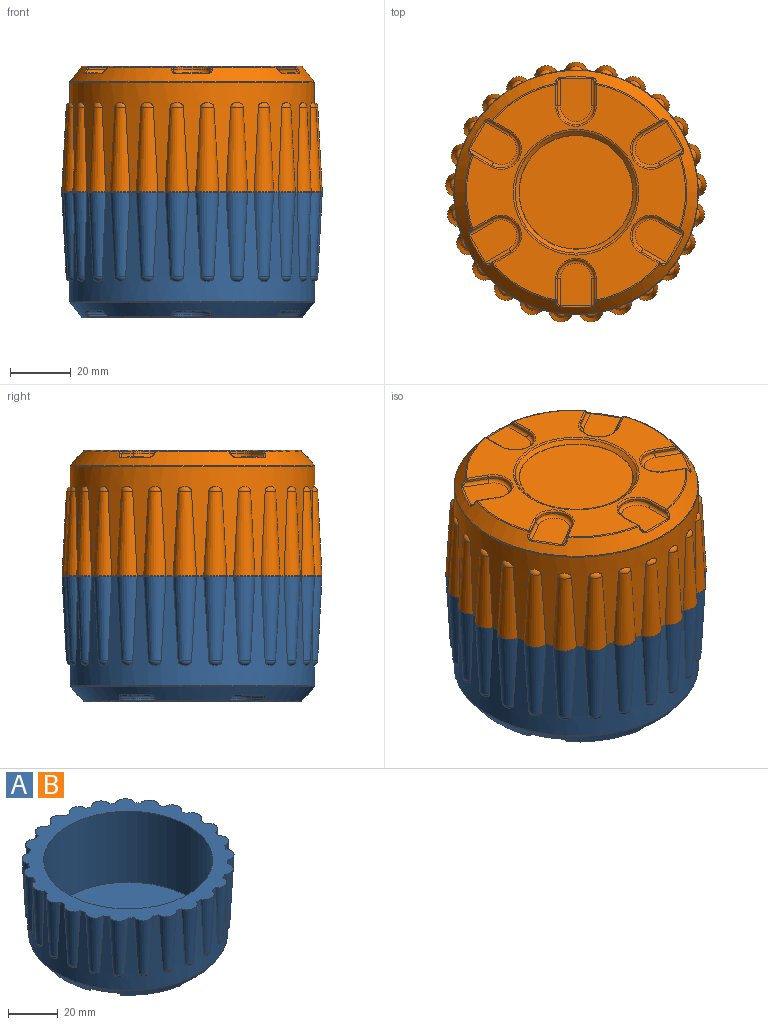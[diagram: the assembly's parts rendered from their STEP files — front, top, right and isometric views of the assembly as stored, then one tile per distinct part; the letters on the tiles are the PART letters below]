
ASSEMBLY  parts=2 mates=1
PART A: 169 faces, bbox 89.4x95.6x46.7 mm
  f0: cylinder r=1.06mm len=8.31mm, axis (0.87,-0.5,0), area 14mm2, adj f1,f5,f6,f148,f152
  f1: torus R=5.1mm, axis (0,0,-1), area 30.2mm2, adj f0,f2,f3,f6
  f2: cylinder r=1.06mm len=8.31mm, axis (-0.87,0.5,0), area 14mm2, adj f1,f4,f6,f148,f153
  f3: cylinder r=6.16mm len=11.5mm, axis (0,0,-1), area 12.8mm2, adj f1,f4,f5,f163
  f4: plane 6.53x3.77mm, normal (0.5,0.87,0), area 4.8mm2, adj f2,f3,f157,f162
  f5: plane 6.53x3.77mm, normal (-0.5,-0.87,0), area 4.8mm2, adj f0,f3,f156,f161
  f6: plane 15.4x14mm, normal (0,0,-1), area 132mm2, adj f0,f1,f2,f148
  f7: cylinder r=1.06mm len=8.31mm, axis (0.87,0.5,0), area 14mm2, adj f8,f12,f13,f140,f144
  f8: torus R=5.1mm, axis (0,0,-1), area 30.2mm2, adj f7,f9,f10,f13
  f9: cylinder r=1.06mm len=8.31mm, axis (-0.87,-0.5,0), area 14mm2, adj f8,f11,f13,f136,f140
  f10: cylinder r=6.16mm len=11.5mm, axis (0,0,-1), area 12.8mm2, adj f8,f11,f12,f145
  f11: plane 6.53x3.77mm, normal (-0.5,0.87,0), area 4.8mm2, adj f9,f10,f132,f141
  f12: plane 6.53x3.77mm, normal (0.5,-0.87,0), area 4.8mm2, adj f7,f10,f149,f150
  f13: plane 15.4x14mm, normal (0,0,-1), area 132mm2, adj f7,f8,f9,f140
  f14: cylinder r=1.06mm len=8.98mm, axis (0,1,0), area 14mm2, adj f15,f19,f20,f118,f122
  f15: torus R=5.1mm, axis (0,0,-1), area 30.2mm2, adj f14,f16,f17,f20
  f16: cylinder r=1.06mm len=8.98mm, axis (0,-1,0), area 14mm2, adj f15,f18,f20,f114,f118
  f17: cylinder r=6.16mm len=12.32mm, axis (0,0,-1), area 12.8mm2, adj f15,f18,f19,f123
  f18: plane 7.54x0.66mm, normal (-1,0,0), area 4.8mm2, adj f16,f17,f110,f119
  f19: plane 7.54x0.66mm, normal (1,0,0), area 4.8mm2, adj f14,f17,f126,f127
  f20: plane 14.04x10.22mm, normal (0,0,-1), area 132mm2, adj f14,f15,f16,f118
  f21: cylinder r=1.06mm len=8.31mm, axis (-0.87,0.5,0), area 14mm2, adj f22,f26,f27,f98,f100
  f22: torus R=5.1mm, axis (0,0,-1), area 30.2mm2, adj f21,f23,f24,f27
  f23: cylinder r=1.06mm len=8.31mm, axis (0.87,-0.5,0), area 14mm2, adj f22,f25,f27,f98,f99
  f24: cylinder r=6.16mm len=11.5mm, axis (0,0,-1), area 12.8mm2, adj f22,f25,f26,f101
  f25: plane 6.53x3.77mm, normal (-0.5,-0.87,0), area 4.8mm2, adj f23,f24,f102,f103
  f26: plane 6.53x3.77mm, normal (0.5,0.87,0), area 4.8mm2, adj f21,f24,f104,f105
  f27: plane 15.4x14mm, normal (0,0,-1), area 132mm2, adj f21,f22,f23,f98
  f28: cylinder r=1.06mm len=8.31mm, axis (-0.87,-0.5,0), area 14mm2, adj f29,f33,f34,f113,f117
  f29: torus R=5.1mm, axis (0,0,-1), area 30.2mm2, adj f28,f30,f31,f34
  f30: cylinder r=1.06mm len=8.31mm, axis (0.87,0.5,0), area 14mm2, adj f29,f32,f34,f117,f121
  f31: cylinder r=6.16mm len=11.5mm, axis (0,0,-1), area 12.8mm2, adj f29,f32,f33,f120
  f32: plane 6.53x3.77mm, normal (0.5,-0.87,0), area 4.8mm2, adj f30,f31,f124,f125
  f33: plane 6.53x3.77mm, normal (-0.5,0.87,0), area 4.8mm2, adj f28,f31,f109,f116
  f34: plane 15.4x14mm, normal (0,0,-1), area 132mm2, adj f28,f29,f30,f117
  f35: cone r=40.23mm half-angle=37.6deg, axis (0,0,1), area 1235.1mm2, adj f98,f99,f100,f103,f104,f108,f109,f110
  f36: plane 72.07x70.83mm, normal (0,0,-1), area 1723.4mm2, adj f101,f102,f105,f108,f111,f116,f119,f120
  f37: plane 68.26x68.26mm, normal (0,0,1), area 3659.7mm2, adj f38
  f38: cylinder r=34.13mm len=68.26mm, axis (0,0,-1), area 7527.1mm2, adj f37,f39
  f39: plane 85.71x85.56mm, normal (0,0,1), area 1809.8mm2, adj f38,f40,f48,f50,f52,f54,f56,f58
  f40: cylinder r=40.23mm len=80.46mm, axis (0,0,-1), area 4744.4mm2, adj f39,f48,f49,f50,f51,f52,f53,f54
  f41: plane 7.54x0.66mm, normal (1,0,0), area 4.8mm2, adj f43,f47,f146,f147
  f42: plane 7.54x0.66mm, normal (-1,0,0), area 4.8mm2, adj f43,f45,f131,f138
  f43: cylinder r=6.16mm len=12.32mm, axis (0,0,-1), area 12.8mm2, adj f41,f42,f46,f142
  f44: plane 14.04x10.22mm, normal (0,0,-1), area 132mm2, adj f45,f46,f47,f139
  f45: cylinder r=1.06mm len=8.98mm, axis (0,-1,0), area 14mm2, adj f42,f44,f46,f135,f139
  f46: torus R=5.1mm, axis (0,0,-1), area 30.2mm2, adj f43,f44,f45,f47
  f47: cylinder r=1.06mm len=8.98mm, axis (0,1,0), area 14mm2, adj f41,f44,f46,f139,f143
  f48: cone r=4mm half-angle=3deg, axis (0,0,1), area 216.4mm2, adj f39,f40,f49
  f49: torus R=1.01mm, axis (0,0,1), area 7.6mm2, adj f40,f48
  f50: cone r=4mm half-angle=3deg, axis (0,0,1), area 216.4mm2, adj f39,f40,f51
  f51: torus R=1.01mm, axis (0,0,1), area 7.6mm2, adj f40,f50
  f52: cone r=4mm half-angle=3deg, axis (0,0,1), area 216.4mm2, adj f39,f40,f53
  f53: torus R=1.01mm, axis (0,0,1), area 7.6mm2, adj f40,f52
  f54: cone r=4mm half-angle=3deg, axis (0,0,1), area 216.4mm2, adj f39,f40,f55
  f55: torus R=1.01mm, axis (0,0,1), area 7.6mm2, adj f40,f54
  f56: cone r=4mm half-angle=3deg, axis (0,0,1), area 216.4mm2, adj f39,f40,f57
  f57: torus R=1.01mm, axis (0,0,1), area 7.6mm2, adj f40,f56
  f58: cone r=4mm half-angle=3deg, axis (0,0,1), area 216.4mm2, adj f39,f40,f59
  f59: torus R=1.01mm, axis (0,0,1), area 7.6mm2, adj f40,f58
  f60: cone r=4mm half-angle=3deg, axis (0,0,1), area 216.4mm2, adj f39,f40,f61
  f61: torus R=1.01mm, axis (0,0,1), area 7.6mm2, adj f40,f60
  f62: cone r=4mm half-angle=3deg, axis (0,0,1), area 216.4mm2, adj f39,f40,f63
  f63: torus R=1.01mm, axis (0,0,1), area 7.6mm2, adj f40,f62
  f64: cone r=4mm half-angle=3deg, axis (0,0,1), area 216.4mm2, adj f39,f40,f65
  f65: torus R=1.01mm, axis (0,0,1), area 7.6mm2, adj f40,f64
  f66: cone r=4mm half-angle=3deg, axis (0,0,1), area 216.4mm2, adj f39,f40,f67
  f67: torus R=1.01mm, axis (0,0,1), area 7.6mm2, adj f40,f66
  f68: cone r=4mm half-angle=3deg, axis (0,0,1), area 216.4mm2, adj f39,f40,f69
  f69: torus R=1.01mm, axis (0,0,1), area 7.6mm2, adj f40,f68
  f70: cone r=4mm half-angle=3deg, axis (0,0,1), area 216.4mm2, adj f39,f40,f71
  f71: torus R=1.01mm, axis (0,0,1), area 7.6mm2, adj f40,f70
  f72: cone r=4mm half-angle=3deg, axis (0,0,1), area 216.4mm2, adj f39,f40,f73
  f73: torus R=1.01mm, axis (0,0,1), area 7.6mm2, adj f40,f72
  f74: cone r=4mm half-angle=3deg, axis (0,0,1), area 216.4mm2, adj f39,f40,f75
  f75: torus R=1.01mm, axis (0,0,1), area 7.6mm2, adj f40,f74
  f76: cone r=4mm half-angle=3deg, axis (0,0,1), area 216.4mm2, adj f39,f40,f77
  f77: torus R=1.01mm, axis (0,0,1), area 7.6mm2, adj f40,f76
  f78: cone r=4mm half-angle=3deg, axis (0,0,1), area 216.4mm2, adj f39,f40,f79
  f79: torus R=1.01mm, axis (0,0,1), area 7.6mm2, adj f40,f78
  f80: cone r=4mm half-angle=3deg, axis (0,0,1), area 216.4mm2, adj f39,f40,f81
  f81: torus R=1.01mm, axis (0,0,1), area 7.6mm2, adj f40,f80
  f82: cone r=4mm half-angle=3deg, axis (0,0,1), area 216.4mm2, adj f39,f40,f83
  f83: torus R=1.01mm, axis (0,0,1), area 7.6mm2, adj f40,f82
  f84: cone r=4mm half-angle=3deg, axis (0,0,1), area 216.4mm2, adj f39,f40,f85
  f85: torus R=1.01mm, axis (0,0,1), area 7.6mm2, adj f40,f84
  f86: cone r=4mm half-angle=3deg, axis (0,0,1), area 216.4mm2, adj f39,f40,f87
  f87: torus R=1.01mm, axis (0,0,1), area 7.6mm2, adj f40,f86
  f88: cone r=4mm half-angle=3deg, axis (0,0,1), area 216.4mm2, adj f39,f40,f89
  f89: torus R=1.01mm, axis (0,0,1), area 7.6mm2, adj f40,f88
  f90: cone r=4mm half-angle=3deg, axis (0,0,1), area 216.4mm2, adj f39,f40,f91
  f91: torus R=1.01mm, axis (0,0,1), area 7.6mm2, adj f40,f90
  f92: cone r=4mm half-angle=3deg, axis (0,0,1), area 216.4mm2, adj f39,f40,f93
  f93: torus R=1.01mm, axis (0,0,1), area 7.6mm2, adj f40,f92
  f94: cone r=4mm half-angle=3deg, axis (0,0,1), area 216.4mm2, adj f39,f40,f95
  f95: torus R=1.01mm, axis (0,0,1), area 7.6mm2, adj f40,f94
  f96: cone r=4mm half-angle=3deg, axis (0,0,1), area 216.4mm2, adj f39,f40,f97
  f97: torus R=1.01mm, axis (0,0,1), area 7.6mm2, adj f40,f96
  f98: bspline ~9.76x5.88mm, area 7.5mm2, adj f21,f23,f27,f35,f99,f100
  f99: bspline ~2.26x1.71mm, area 1.6mm2, adj f23,f35,f98,f103
  f100: bspline ~2.27x1.71mm, area 1.6mm2, adj f21,f35,f98,f104
  f101: torus R=6.66mm, axis (0,0,1), area 15.7mm2, adj f24,f36,f102,f105
  f102: cylinder r=0.5mm len=6.33mm, axis (0.87,-0.5,0), area 5.5mm2, adj f25,f36,f101,f106
  f103: bspline ~21.11x14.68mm, area 0.7mm2, adj f25,f35,f99,f106
  f104: bspline ~21.11x14.45mm, area 0.7mm2, adj f26,f35,f100,f107
  f105: cylinder r=0.5mm len=6.33mm, axis (-0.87,0.5,0), area 5.5mm2, adj f26,f36,f101,f107
  f106: sphere r=0.5mm, area 0.3mm2, adj f102,f103,f108
  f107: sphere r=0.5mm, area 0.1mm2, adj f104,f105,f111
  f108: torus R=36.04mm, axis (0,0,1), area 11.2mm2, adj f35,f36,f106,f112
  f109: bspline ~21.11x14.68mm, area 0.7mm2, adj f33,f35,f112,f113
  f110: bspline ~21.11x16.68mm, area 0.7mm2, adj f18,f35,f114,f115
  f111: torus R=36.04mm, axis (0,0,1), area 11.2mm2, adj f35,f36,f107,f115
  f112: sphere r=0.5mm, area 0.3mm2, adj f108,f109,f116
  f113: bspline ~2.26x1.71mm, area 1.6mm2, adj f28,f35,f109,f117
  f114: bspline ~1.97x1.71mm, area 1.6mm2, adj f16,f35,f110,f118
  f115: sphere r=0.5mm, area 0.3mm2, adj f110,f111,f119
  f116: cylinder r=0.5mm len=6.33mm, axis (-0.87,-0.5,0), area 5.5mm2, adj f33,f36,f112,f120
  f117: bspline ~9.29x5.62mm, area 7.5mm2, adj f28,f30,f34,f35,f113,f121
  f118: bspline ~11.1x0.72mm, area 7.5mm2, adj f14,f16,f20,f35,f114,f122
  f119: cylinder r=0.5mm len=7.02mm, axis (0,-1,0), area 5.5mm2, adj f18,f36,f115,f123
  f120: torus R=6.66mm, axis (0,0,1), area 15.7mm2, adj f31,f36,f116,f124
  f121: bspline ~2.27x1.71mm, area 1.6mm2, adj f30,f35,f117,f125
  f122: bspline ~1.97x1.71mm, area 1.6mm2, adj f14,f35,f118,f126
  f123: torus R=6.66mm, axis (0,0,1), area 15.7mm2, adj f17,f36,f119,f127
  f124: cylinder r=0.5mm len=6.33mm, axis (0.87,0.5,0), area 5.5mm2, adj f32,f36,f120,f128
  f125: bspline ~21.11x14.45mm, area 0.7mm2, adj f32,f35,f121,f128
  f126: bspline ~21.11x16.68mm, area 0.7mm2, adj f19,f35,f122,f129
  f127: cylinder r=0.5mm len=7.02mm, axis (0,1,0), area 5.5mm2, adj f19,f36,f123,f129
  f128: sphere r=0.5mm, area 0.1mm2, adj f124,f125,f130
  f129: sphere r=0.5mm, area 0.2mm2, adj f126,f127,f133
  f130: torus R=36.04mm, axis (0,0,1), area 11.2mm2, adj f35,f36,f128,f134
  f131: bspline ~21.11x16.68mm, area 0.7mm2, adj f35,f42,f134,f135
  f132: bspline ~21.11x14.45mm, area 0.7mm2, adj f11,f35,f136,f137
  f133: torus R=36.04mm, axis (0,0,1), area 11.2mm2, adj f35,f36,f129,f137
  f134: sphere r=0.5mm, area 0.3mm2, adj f130,f131,f138
  f135: bspline ~1.97x1.71mm, area 1.6mm2, adj f35,f45,f131,f139
  f136: bspline ~2.27x1.71mm, area 1.6mm2, adj f9,f35,f132,f140
  f137: sphere r=0.5mm, area 0.3mm2, adj f132,f133,f141
  f138: cylinder r=0.5mm len=7.02mm, axis (0,-1,0), area 5.5mm2, adj f36,f42,f134,f142
  f139: bspline ~11.1x0.72mm, area 7.5mm2, adj f35,f44,f45,f47,f135,f143
  f140: bspline ~9.29x5.62mm, area 7.5mm2, adj f7,f9,f13,f35,f136,f144
  f141: cylinder r=0.5mm len=6.33mm, axis (-0.87,-0.5,0), area 5.5mm2, adj f11,f36,f137,f145
  f142: torus R=6.66mm, axis (0,0,1), area 15.7mm2, adj f36,f43,f138,f146
  f143: bspline ~1.97x1.71mm, area 1.6mm2, adj f35,f47,f139,f147
  f144: bspline ~2.26x1.71mm, area 1.6mm2, adj f7,f35,f140,f149
  f145: torus R=6.66mm, axis (0,0,1), area 15.7mm2, adj f10,f36,f141,f150
  f146: cylinder r=0.5mm len=7.02mm, axis (0,1,0), area 5.5mm2, adj f36,f41,f142,f151
  f147: bspline ~21.11x16.68mm, area 0.7mm2, adj f35,f41,f143,f151
  f148: bspline ~9.76x5.88mm, area 7.5mm2, adj f0,f2,f6,f35,f152,f153
  f149: bspline ~21.11x14.68mm, area 0.7mm2, adj f12,f35,f144,f154
  f150: cylinder r=0.5mm len=6.33mm, axis (0.87,0.5,0), area 5.5mm2, adj f12,f36,f145,f154
  f151: sphere r=0.5mm, area 0.2mm2, adj f146,f147,f155
  f152: bspline ~2.27x1.71mm, area 1.6mm2, adj f0,f35,f148,f156
  f153: bspline ~2.26x1.71mm, area 1.6mm2, adj f2,f35,f148,f157
  f154: sphere r=0.5mm, area 0.3mm2, adj f149,f150,f158
  f155: torus R=36.04mm, axis (0,0,1), area 11.2mm2, adj f35,f36,f151,f159
  f156: bspline ~21.11x14.45mm, area 0.7mm2, adj f5,f35,f152,f159
  f157: bspline ~21.11x14.68mm, area 0.7mm2, adj f4,f35,f153,f160
  f158: torus R=36.04mm, axis (0,0,1), area 11.2mm2, adj f35,f36,f154,f160
  f159: sphere r=0.5mm, area 0.3mm2, adj f155,f156,f161
  f160: sphere r=0.5mm, area 0.3mm2, adj f157,f158,f162
  f161: cylinder r=0.5mm len=6.33mm, axis (0.87,-0.5,0), area 5.5mm2, adj f5,f36,f159,f163
  f162: cylinder r=0.5mm len=6.33mm, axis (-0.87,0.5,0), area 5.5mm2, adj f4,f36,f160,f163
  f163: torus R=6.66mm, axis (0,0,1), area 15.7mm2, adj f3,f36,f161,f162
  f164: torus R=39.73mm, axis (0,0,1), area 83mm2, adj f35,f40
  f165: plane 37.33x37.33mm, normal (0,0,-1), area 1094.5mm2, adj f168
  f166: cone r=18.67mm half-angle=47.5deg, axis (0,0,-1), area 211.7mm2, adj f167,f168
  f167: torus R=20.69mm, axis (0,0,1), area 94.8mm2, adj f36,f166
  f168: torus R=19.4mm, axis (0,0,1), area 10.3mm2, adj f165,f166
PART B: same geometry as A
PLACE A t=(-24.22,4.15,6.77)mm
PLACE B rot(axis=(0,1,0),180deg) t=(-24.22,4.15,89.41)mm
MATE slider B.f35 <-> A.f35  axis (0,0,1) through (-24.22,4.15,48.09)mm
